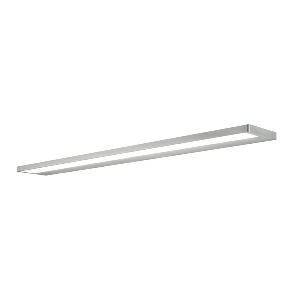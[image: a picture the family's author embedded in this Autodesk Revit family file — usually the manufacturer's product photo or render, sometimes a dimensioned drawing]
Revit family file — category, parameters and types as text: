
# Revit family: zera_wall_-_zew_6000_830_d_00812393_c276
name_source: partatom
category: Lighting Fixtures
units: mm (PartAtom-declared; Revit-internal decimal feet)

## family parameters
Cut with Voids When Loaded = No
Host = Face
Light Source = No
Part Type = Normal
Room Calculation Point = No
Round Connector Dimension = Use Diameter
Shared = No

## types (1)
- ZERA.wall - ZEW 6000/830/D (1 x LED, 5600 lm, 3000K)
    Apparent Load = 40 VA
    Approval mark = CE
    CIE Flux Codes = 46 78 95 41 100
    Color Rendering = 80-89
    Color Temperature = 3000K
    Control Gear = Electronic ballast
    Default Elevation = 2000 mm  [stored 6.56168 ft]
    Description = ZEW 6000/830/D|Wall-mounted luminaire|light source:   Warm white   |work equipment: Electronic ballast dimable digital|luminous flux: 5600 lm|light distribution: Direct/indirect|class of protection: I|technology: Continuously dimmable|mains lead: Connector 5 pin|glare control: Diffusor|special features: Asymmetric radiation, DALI Load 1x, DIN EN 60598-2-25, Integration into DALI light management systems, Suitable as emergency lighting|
    Frequency = 50 Hz, 60 Hz
    Height = 29 mm
    Lamp = 1 x LED
    Lamp Light Flux = 5600 lm
    Lamp count = 1
    Length = 1050 mm
    Luminous efficacy = 140 lm/W
    Manufacturer = Waldmann
    ModVariant = No
    Model = 00812393
    Mounting Place = Wall
    Mounting Type = Surface mounted
    Number of Poles = 1
    OnlyDefault = Yes
    Power Factor = 1
    Product Name = ZERA.wall - ZEW 6000/830/D
    Product group = Wall mounted Luminaire
    ProductGroupID = 20
    Protection Class = Protection class I
    Protection Degree = IP 20
    RLX_Detail_Level = 1
    RLX_Emergency_Light_Flux = 0 lm
    RLX_Emergency_Type = 0
    RLX_Emergency_Type_DB = No
    RlxData = <blob elided: 33361 chars, md5=566928ca>
    Socket = socket
    Standby Power = 0 W
    System Light Flux = 5600 lm
    System Power = 40 W
    Type Comments = Product without accessories
    Type Image = zera_40_w.jpg
    URL = http://relux.com
    VarID = ---
    Voltage = 230 V
    Voltage Range = 220-240 V
    Weight = 0.00 kg
    Width = 142 mm

note: [stored X ft] marks values corroborated as IEEE doubles in the binary element streams (Revit-internal decimal feet)

## geometry (parser evidence)
native form markers: Blend x4, Sweep x13
no freeform markers — native parametric forms only
